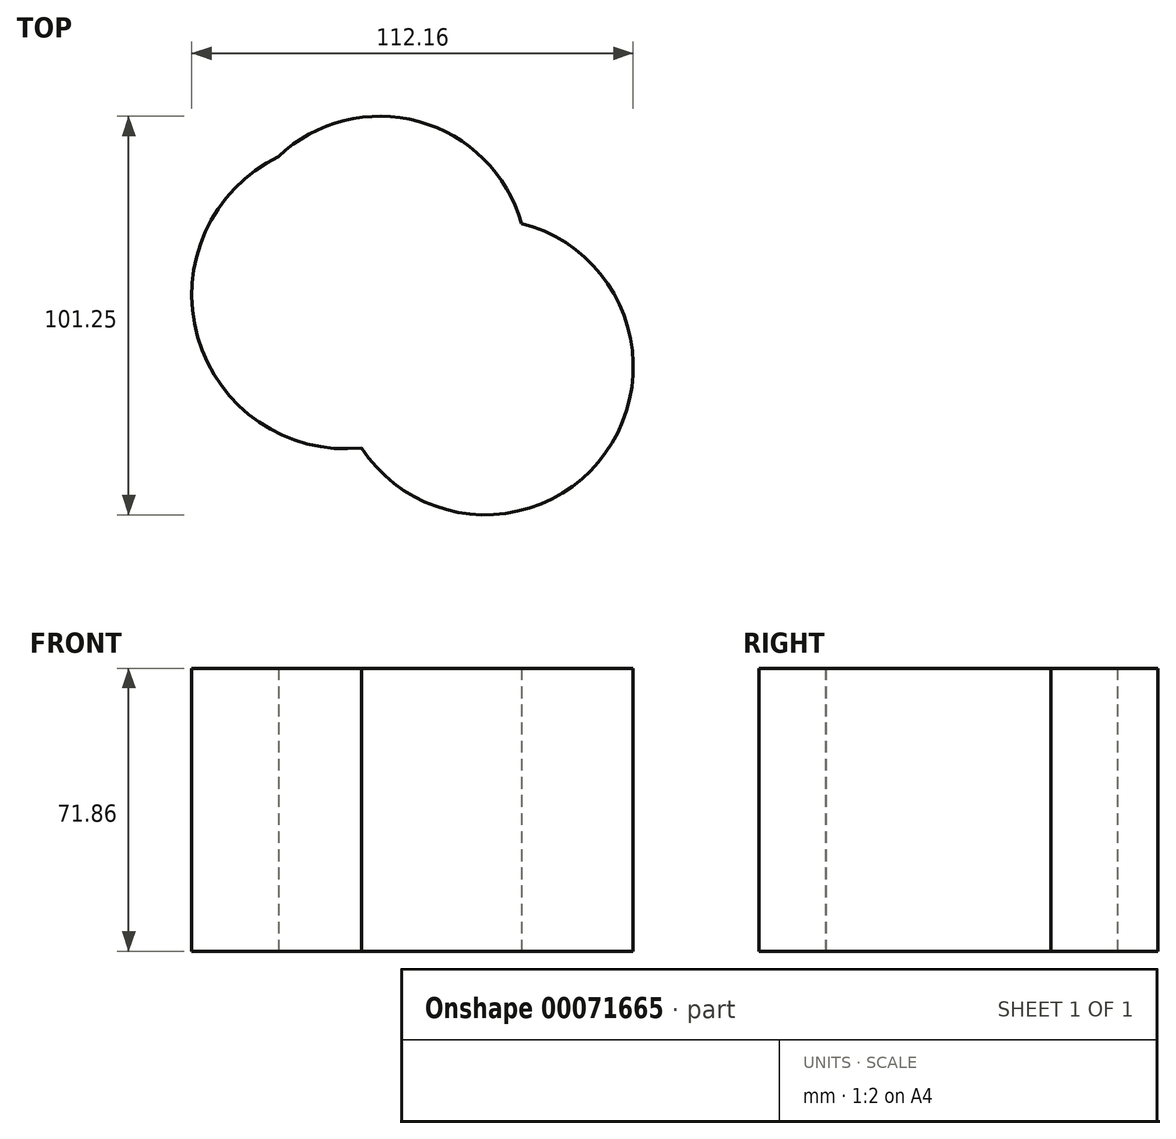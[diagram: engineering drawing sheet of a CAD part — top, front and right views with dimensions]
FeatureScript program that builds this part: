
annotation { "Feature Type Name" : "Feature", "Feature Type Description" : "" }
export const myFeature = defineFeature(function(context is Context, id is Id, definition is map)
    precondition{}
    {
        {
            var Q0;
            Q0=qCreatedBy(makeId("Top.planeOp"),FACE);
            var sketch = newSketch(context, id + "F0", { "sketchPlane" : qUnion([Q0])});
            skCircle(sketch, "E0", {"center": v(-67.55, 18.9) * mm, "radius": 37.46 * mm});
            skCircle(sketch, "E1", {"center": v(-40.77, -7.3) * mm, "radius": 37.6 * mm});
            skCircle(sketch, "E2", {"center": v(-76.25, 10.96) * mm, "radius": 39.07 * mm});
            skPoint(sketch, "E2.first.point", {"position": v(-93.26, 46.13) * mm});
            skPoint(sketch, "E2.second.point", {"position": v(-42.8, -9.22) * mm});
            skPoint(sketch, "E2.third.point", {"position": v(-58.32, 45.68) * mm});
            skSolve(sketch);
        }
        {
            var Q0;
            {var subQ0=sQuery(id+"F0.wireOp",EDGE,"E2");var subQ1=sQuery(id+"F0.wireOp",EDGE,"E0");var subQ2=makeQuery(id+"F0.imprint","INTERSECT",VERTEX,{"disambiguationData":[OD(0.0)],"derivedFrom":[subQ1,subQ0]});Q0=makeQuery(id+"F0.imprint","IMPRINT",FACE,{"disambiguationData":[TD([[makeQuery(id+"F0.imprint","IMPRINT",EDGE,{"disambiguationData":[TD([[subQ2,1.0]])],"derivedFrom":subQ1}),1.0]])]});}
            var Q1;
            {var subQ0=sQuery(id+"F0.wireOp",EDGE,"E2");var subQ1=sQuery(id+"F0.wireOp",EDGE,"E0");var subQ2=makeQuery(id+"F0.imprint","INTERSECT",VERTEX,{"disambiguationData":[OD(0.0)],"derivedFrom":[subQ1,subQ0]});Q1=makeQuery(id+"F0.imprint","IMPRINT",FACE,{"disambiguationData":[TD([[makeQuery(id+"F0.imprint","IMPRINT",EDGE,{"disambiguationData":[TD([[subQ2,-1.0]])],"derivedFrom":subQ1}),-1.0]])]});}
            var Q2;
            {var subQ0=sQuery(id+"F0.wireOp",EDGE,"E1");var subQ1=sQuery(id+"F0.wireOp",EDGE,"E0");var subQ2=makeQuery(id+"F0.imprint","INTERSECT",VERTEX,{"disambiguationData":[OD(0.0)],"derivedFrom":[subQ1,subQ0]});Q2=makeQuery(id+"F0.imprint","IMPRINT",FACE,{"disambiguationData":[TD([[makeQuery(id+"F0.imprint","IMPRINT",EDGE,{"disambiguationData":[TD([[subQ2,1.0]])],"derivedFrom":subQ1}),-1.0]])]});}
            var Q3;
            {var subQ0=sQuery(id+"F0.wireOp",EDGE,"E2");var subQ1=sQuery(id+"F0.wireOp",EDGE,"E0");var subQ2=makeQuery(id+"F0.imprint","INTERSECT",VERTEX,{"disambiguationData":[OD(0.0)],"derivedFrom":[subQ1,subQ0]});Q3=makeQuery(id+"F0.imprint","IMPRINT",FACE,{"disambiguationData":[TD([[makeQuery(id+"F0.imprint","IMPRINT",EDGE,{"disambiguationData":[TD([[subQ2,-1.0]])],"derivedFrom":subQ1}),1.0]])]});}
            var Q4;
            {var subQ0=sQuery(id+"F0.wireOp",EDGE,"E1");var subQ1=sQuery(id+"F0.wireOp",EDGE,"E0");var subQ2=makeQuery(id+"F0.imprint","INTERSECT",VERTEX,{"disambiguationData":[OD(1.0)],"derivedFrom":[subQ1,subQ0]});Q4=makeQuery(id+"F0.imprint","IMPRINT",FACE,{"disambiguationData":[TD([[makeQuery(id+"F0.imprint","IMPRINT",EDGE,{"disambiguationData":[TD([[subQ2,-1.0]])],"derivedFrom":subQ1}),-1.0]])]});}
            var Q5;
            {var subQ0=sQuery(id+"F0.wireOp",EDGE,"E1");var subQ1=sQuery(id+"F0.wireOp",EDGE,"E0");var subQ2=makeQuery(id+"F0.imprint","INTERSECT",VERTEX,{"disambiguationData":[OD(0.0)],"derivedFrom":[subQ1,subQ0]});Q5=makeQuery(id+"F0.imprint","IMPRINT",FACE,{"disambiguationData":[TD([[makeQuery(id+"F0.imprint","IMPRINT",EDGE,{"disambiguationData":[TD([[subQ2,1.0]])],"derivedFrom":subQ1}),1.0]])]});}
            var Q6;
            Q6 = qSketchRegion(id + "FBqqsyfrztHQoFu_0", true);
            var Q7;
            {var subQ0=sQuery(id+"F0.wireOp",EDGE,"E1");var subQ1=sQuery(id+"F0.wireOp",EDGE,"E0");var subQ2=makeQuery(id+"F0.imprint","INTERSECT",VERTEX,{"disambiguationData":[OD(1.0)],"derivedFrom":[subQ1,subQ0]});Q7=makeQuery(id+"F0.imprint","IMPRINT",FACE,{"disambiguationData":[TD([[makeQuery(id+"F0.imprint","IMPRINT",EDGE,{"disambiguationData":[TD([[subQ2,-1.0]])],"derivedFrom":subQ1}),1.0]])]});}
            extrude(context, id + "F1", {"entities" : qUnion([Q0, Q1, Q2, Q3, Q4, Q5, Q6, Q7]), "depth" : 71.86 * mm});
        }
    });
